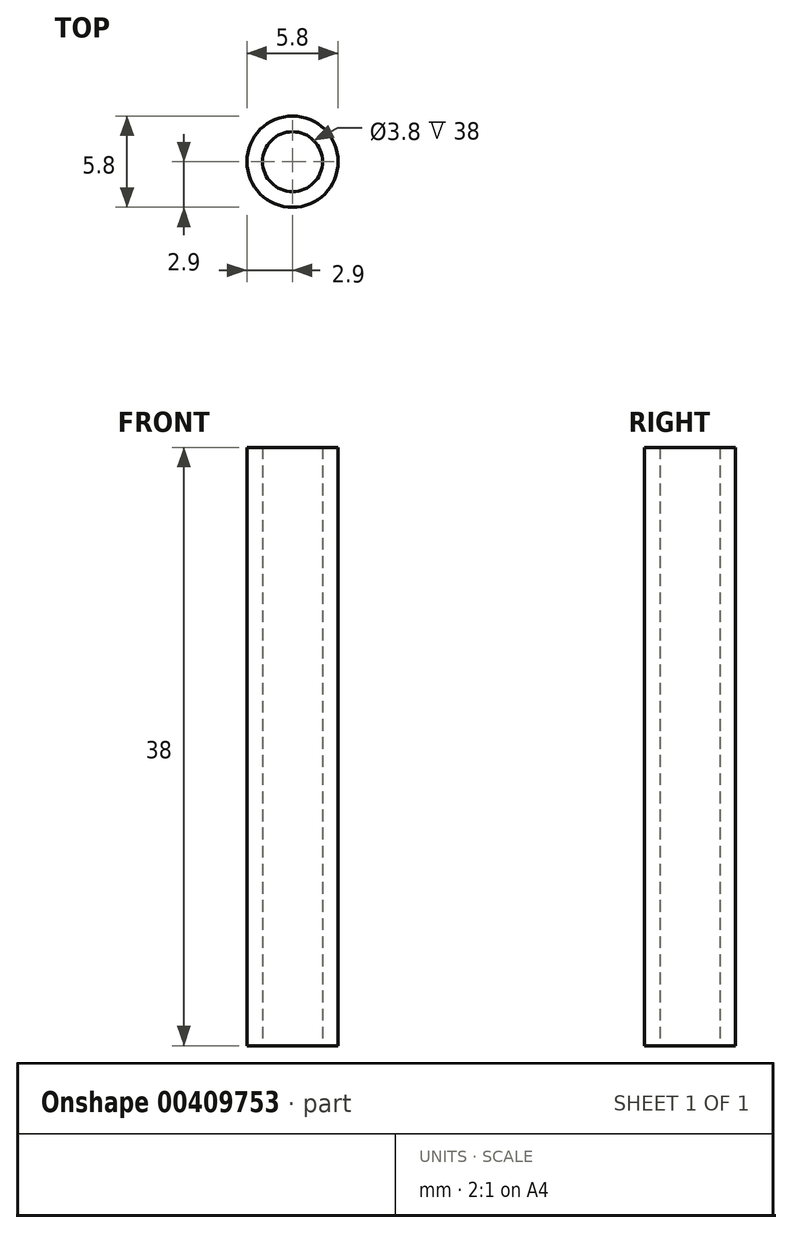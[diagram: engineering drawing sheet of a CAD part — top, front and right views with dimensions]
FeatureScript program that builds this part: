
annotation { "Feature Type Name" : "Feature", "Feature Type Description" : "" }
export const myFeature = defineFeature(function(context is Context, id is Id, definition is map)
    precondition{}
    {
        {
            var Q0;
            Q0=qCreatedBy(makeId("Top.planeOp"),FACE);
            var sketch = newSketch(context, id + "F0", { "sketchPlane" : qUnion([Q0])});
            skCircle(sketch, "E0", {"center": v(0, 0) * mm, "radius": 1.9 * mm});
            skCircle(sketch, "E1", {"center": v(0, 0) * mm, "radius": 2.9 * mm});
            skSolve(sketch);
        }
        {
            var Q0;
            Q0=makeQuery(id+"F0.imprint","IMPRINT",FACE,{"disambiguationData":[TD([[makeQuery(id+"F0.imprint","IMPRINT",EDGE,{"derivedFrom":sQuery(id+"F0.wireOp",EDGE,"E0")}),-1.0]])]});
            extrude(context, id + "F1", {"entities" : qUnion([Q0]), "depth" : 38 * mm});
        }
    });
